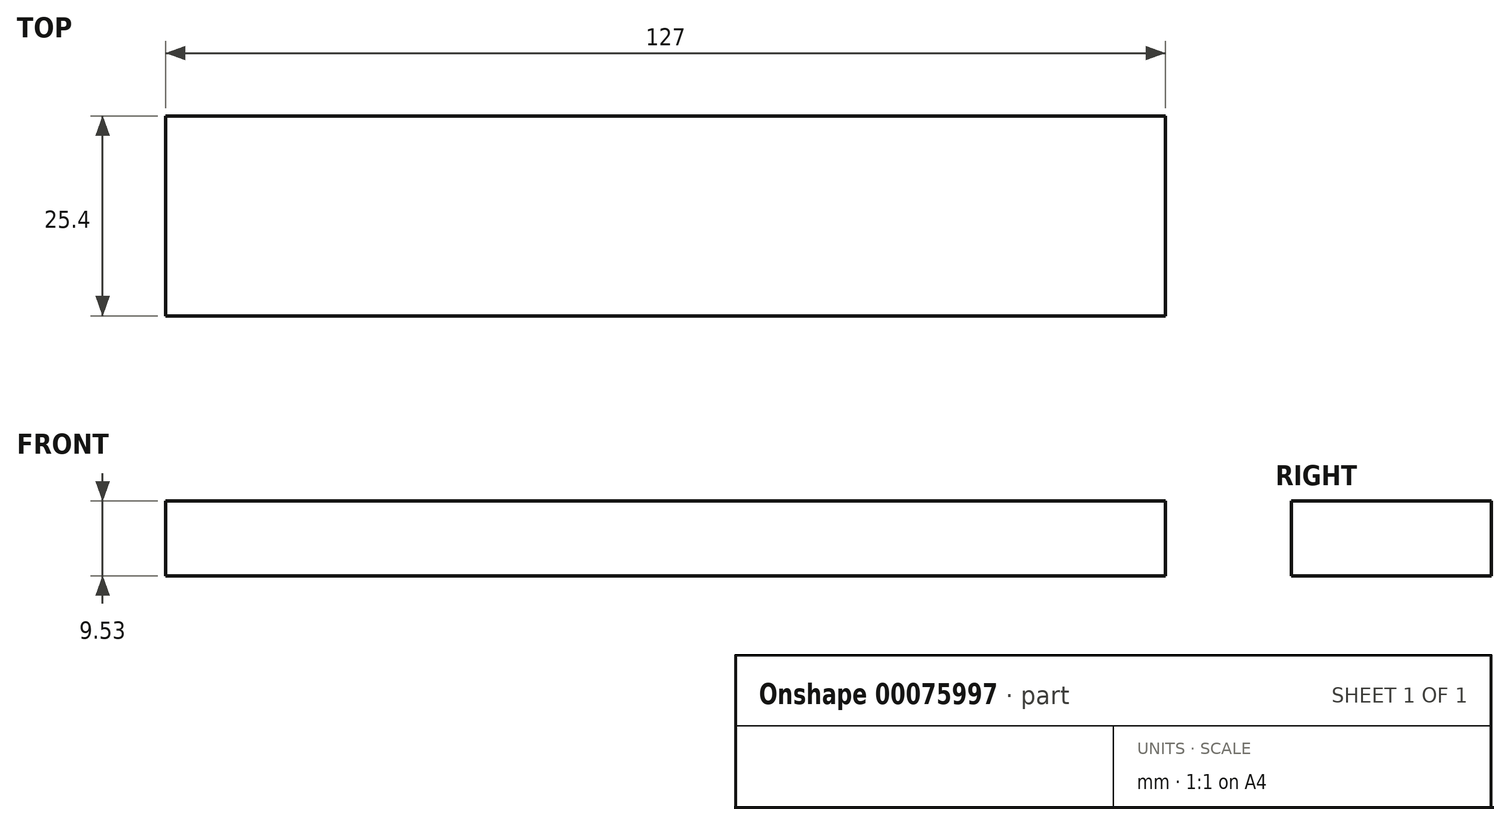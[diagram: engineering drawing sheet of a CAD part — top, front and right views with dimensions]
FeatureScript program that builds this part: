
annotation { "Feature Type Name" : "Feature", "Feature Type Description" : "" }
export const myFeature = defineFeature(function(context is Context, id is Id, definition is map)
    precondition{}
    {
        {
            var Q0;
            Q0=qCreatedBy(makeId("Top.planeOp"),FACE);
            var sketch = newSketch(context, id + "F0", { "sketchPlane" : qUnion([Q0])});
            skLineSegment(sketch, "E0.bottom", {"start": v(63.5, -12.7) * mm, "end": v(-63.5, -12.7) * mm});
            skLineSegment(sketch, "E0.top", {"start": v(63.5, 12.7) * mm, "end": v(-63.5, 12.7) * mm});
            skLineSegment(sketch, "E0.left", {"start": v(63.5, -12.7) * mm, "end": v(63.5, 12.7) * mm});
            skLineSegment(sketch, "E0.right", {"start": v(-63.5, -12.7) * mm, "end": v(-63.5, 12.7) * mm});
            skPoint(sketch, "E0.middle", {"position": v(0, 0) * mm});
            skSolve(sketch);
        }
        {
            var Q0;
            Q0 = qSketchRegion(id + "F0", true);
            extrude(context, id + "F1", {"entities" : qUnion([Q0]), "depth" : 9.52 * mm});
        }
    });
